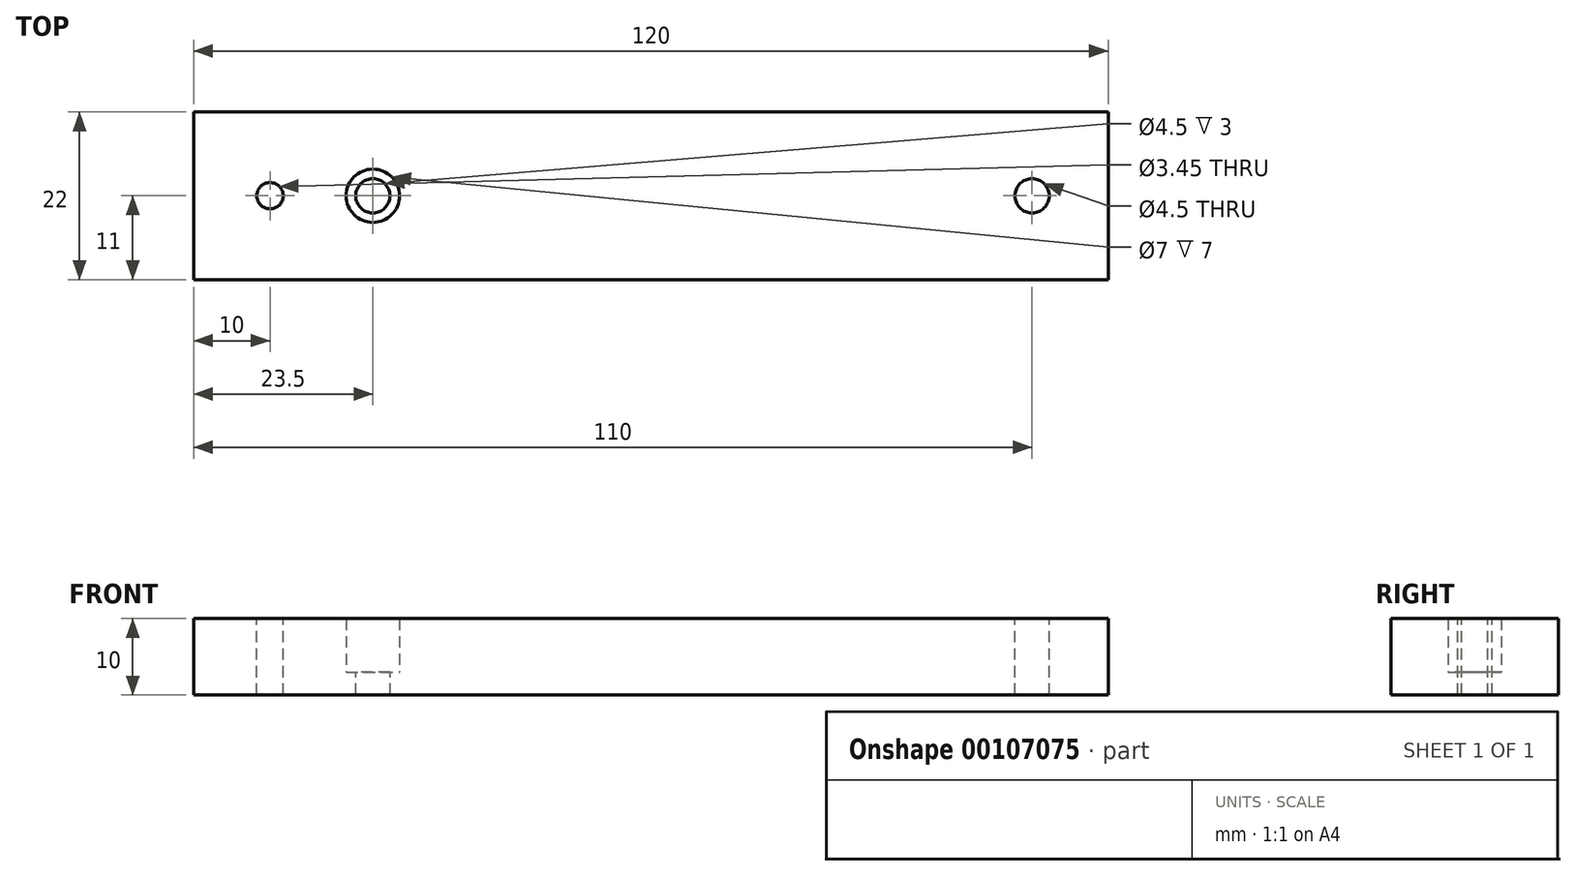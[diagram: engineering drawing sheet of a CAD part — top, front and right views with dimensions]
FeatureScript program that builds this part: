
annotation { "Feature Type Name" : "Feature", "Feature Type Description" : "" }
export const myFeature = defineFeature(function(context is Context, id is Id, definition is map)
    precondition{}
    {
        {
            var Q0;
            Q0=qCreatedBy(makeId("Top.planeOp"),FACE);
            var sketch = newSketch(context, id + "F0", { "sketchPlane" : qUnion([Q0])});
            skLineSegment(sketch, "E0.bottom", {"start": v(60, -11) * mm, "end": v(-60, -11) * mm});
            skLineSegment(sketch, "E0.top", {"start": v(60, 11) * mm, "end": v(-60, 11) * mm});
            skLineSegment(sketch, "E0.left", {"start": v(60, -11) * mm, "end": v(60, 11) * mm});
            skLineSegment(sketch, "E0.right", {"start": v(-60, -11) * mm, "end": v(-60, 11) * mm});
            skPoint(sketch, "E0.middle", {"position": v(0, 0) * mm});
            skSolve(sketch);
        }
        {
            var Q0;
            Q0 = qSketchRegion(id + "F0", true);
            extrude(context, id + "F1", {"entities" : qUnion([Q0]), "depth" : 10 * mm});
        }
        {
            var Q0;
            Q0=makeQuery(id+"F1.opExtrude","CAP_FACE",FACE,{"disambiguationData":[OSD([sQuery(id+"F0.wireOp",EDGE,"E0.bottom"),sQuery(id+"F0.wireOp",EDGE,"E0.top"),sQuery(id+"F0.wireOp",EDGE,"E0.left"),sQuery(id+"F0.wireOp",EDGE,"E0.right")])],"isStart":false});
            var sketch = newSketch(context, id + "F2", { "sketchPlane" : qUnion([Q0])});
            skLineSegment(sketch, "E1", {"start": v(0, 0) * mm, "end": v(-50, 0) * mm, "construction": true});
            skSolve(sketch);
        }
        {
            var Q0;
            Q0=sQuery(id+"F2.wireOp",VERTEX,"E1.end");
            var Q1;
            Q1=makeQuery(id+"F1.opExtrude","SWEPT_BODY",BODY,{"disambiguationData":[OSD([sQuery(id+"F0.wireOp",EDGE,"E0.bottom"),sQuery(id+"F0.wireOp",EDGE,"E0.top"),sQuery(id+"F0.wireOp",EDGE,"E0.left"),sQuery(id+"F0.wireOp",EDGE,"E0.right")])]});
            hole(context, id + "F3", {"style" : HoleStyle.SIMPLE, "endStyle" : HoleEndStyle.THROUGH, "standardTappedOrClearance" : lookupTablePath({ "standard" : "ANSI", "engagement" : "75%", "pitch" : "32 tpi", "size" : "#8", "type" : "Tapped" }), "standardBlindInLast" : lookupTablePath({ "standard" : "ANSI", "engagement" : "75%", "pitch" : "32 tpi", "size" : "#8", "type" : "Tapped" }), "holeDiameter" : 3.45 * mm, "startFromSketch" : true, "locations" : qUnion([Q0]), "scope" : qUnion([Q1]), "isTappedThrough" : true, "majorDiameter" : 4.17 * mm, "showTappedDepth" : true});
        }
        {
            var Q0;
            Q0=makeQuery(id+"F2.imprint","IMPRINT",FACE,{"disambiguationData":[TD([[makeQuery(id+"F2.imprint","IMPRINT",EDGE,{"derivedFrom":makeQuery(id+"F1.opExtrude","CAP_EDGE",EDGE,{"disambiguationData":[OSD([sQuery(id+"F0.wireOp",EDGE,"E0.bottom")])],"isStart":false})}),-1.0]])]});
            var sketch = newSketch(context, id + "F4", { "sketchPlane" : qUnion([Q0])});
            skLineSegment(sketch, "E2", {"start": v(0, 0) * mm, "end": v(50, 0) * mm, "construction": true});
            skLineSegment(sketch, "E3", {"start": v(0, 0) * mm, "end": v(-36.5, 0) * mm, "construction": true});
            skSolve(sketch);
        }
        {
            var Q0;
            Q0=sQuery(id+"F4.wireOp",VERTEX,"E3.end");
            var Q1;
            Q1=sQuery(id+"F4.wireOp",VERTEX,"E2.end");
            var Q2;
            Q2=makeQuery(id+"F1.opExtrude","SWEPT_BODY",BODY,{"disambiguationData":[OSD([sQuery(id+"F0.wireOp",EDGE,"E0.bottom"),sQuery(id+"F0.wireOp",EDGE,"E0.top"),sQuery(id+"F0.wireOp",EDGE,"E0.left"),sQuery(id+"F0.wireOp",EDGE,"E0.right")])]});
            hole(context, id + "F5", {"style" : HoleStyle.SIMPLE, "endStyle" : HoleEndStyle.THROUGH, "standardTappedOrClearance" : lookupTablePath({ "standard" : "ANSI", "fit" : "Normal (ASME)", "size" : "#8", "type" : "Clearance" }), "standardBlindInLast" : lookupTablePath({ "fit" : "Free", "standard" : "ANSI", "size" : "#8", "type" : "Clearance" }), "holeDiameter" : 4.5 * mm, "startFromSketch" : true, "locations" : qUnion([Q0, Q1]), "scope" : qUnion([Q2]), "isTappedThrough" : true});
        }
        {
            var Q0;
            Q0=qCreatedBy(makeId("Front.planeOp"),FACE);
            var sketch = newSketch(context, id + "F6", { "sketchPlane" : qUnion([Q0])});
            skLineSegment(sketch, "E4", {"start": v(-36.5, 10) * mm, "end": v(-36.5, 0) * mm, "construction": true});
            skLineSegment(sketch, "E5.bottom", {"start": v(-33, 3) * mm, "end": v(-35.5, 3) * mm});
            skLineSegment(sketch, "E5.top", {"start": v(-33, 10) * mm, "end": v(-35.5, 10) * mm});
            skLineSegment(sketch, "E5.left", {"start": v(-33, 3) * mm, "end": v(-33, 10) * mm});
            skLineSegment(sketch, "E5.right", {"start": v(-35.5, 3) * mm, "end": v(-35.5, 10) * mm});
            skSolve(sketch);
        }
        {
            var Q0;
            Q0 = qSketchRegion(id + "F6", true);
            var Q1;
            Q1=sQuery(id+"F6.wireOp",EDGE,"E4");
            revolve(context, id + "F7", {"operationType" : NewBodyOperationType.REMOVE, "entities" : qUnion([Q0]), "axis" : qUnion([Q1]), "revolveType" : RevolveType.FULL, "oppositeDirection" : true});
        }
    });
